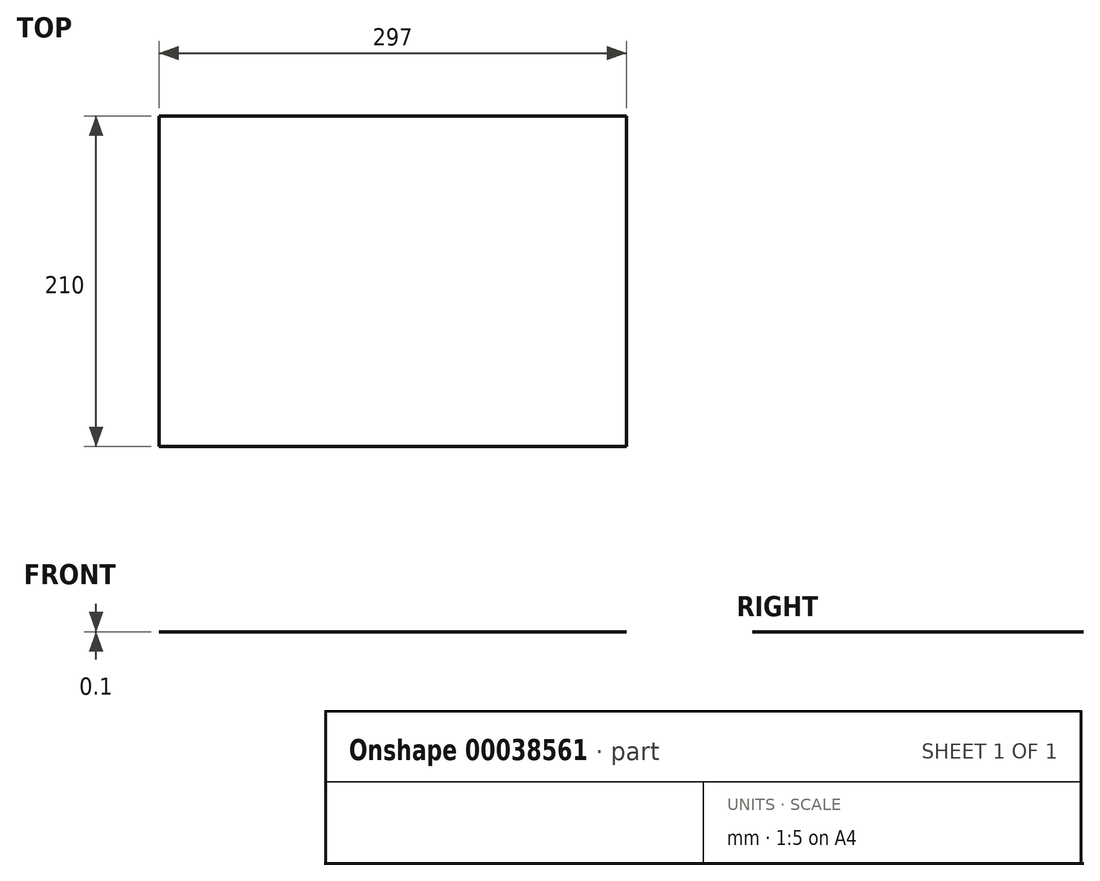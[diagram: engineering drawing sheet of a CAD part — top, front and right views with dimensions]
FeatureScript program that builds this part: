
annotation { "Feature Type Name" : "Feature", "Feature Type Description" : "" }
export const myFeature = defineFeature(function(context is Context, id is Id, definition is map)
    precondition{}
    {
        {
            var Q0;
            Q0=qCreatedBy(makeId("Top.planeOp"),FACE);
            var sketch = newSketch(context, id + "F0", { "sketchPlane" : qUnion([Q0])});
            skLineSegment(sketch, "E0.rect.bottom", {"start": v(-148.5, -105) * mm, "end": v(148.5, -105) * mm});
            skLineSegment(sketch, "E0.rect.top", {"start": v(-148.5, 105) * mm, "end": v(148.5, 105) * mm});
            skLineSegment(sketch, "E0.rect.left", {"start": v(-148.5, -105) * mm, "end": v(-148.5, 105) * mm});
            skLineSegment(sketch, "E0.rect.right", {"start": v(148.5, -105) * mm, "end": v(148.5, 105) * mm});
            skPoint(sketch, "E0.rect.middle", {"position": v(0, 0) * mm});
            skSolve(sketch);
        }
        {
            var Q0;
            Q0=makeQuery(id+"F0.imprint","IMPRINT",FACE,{"disambiguationData":[TD([[makeQuery(id+"F0.imprint","IMPRINT",EDGE,{"derivedFrom":sQuery(id+"F0.wireOp",EDGE,"E0.rect.bottom")}),1.0]])]});
            extrude(context, id + "F1", {"entities" : qUnion([Q0]), "depth" : 0.1 * mm});
        }
    });
